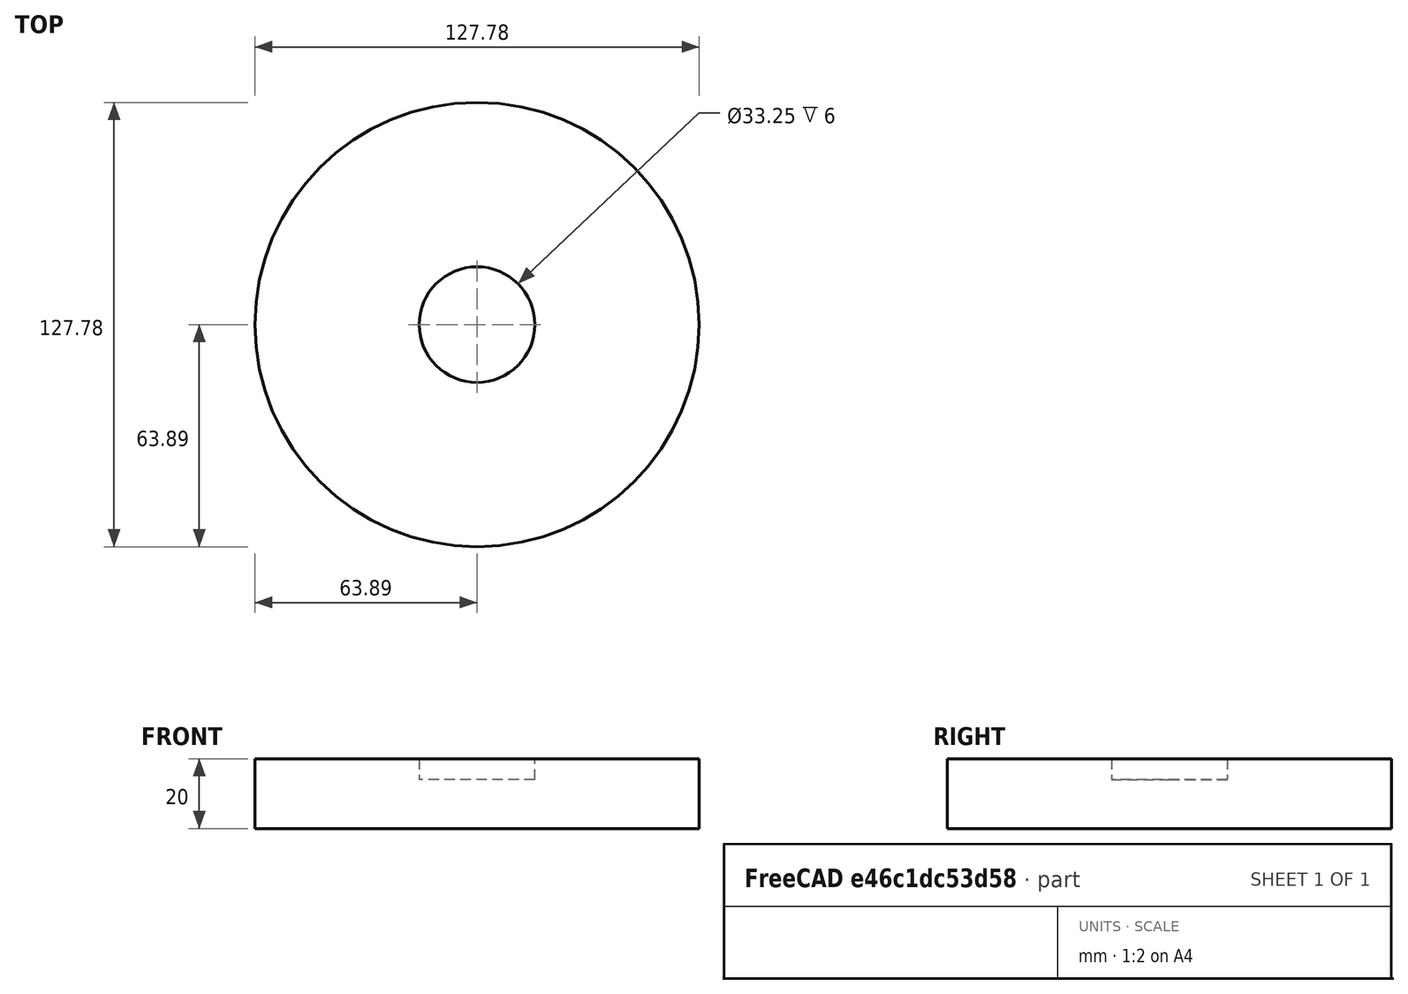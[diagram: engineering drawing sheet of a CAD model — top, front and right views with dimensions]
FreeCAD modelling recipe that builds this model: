
FCSTD DOCUMENT  (FreeCAD 0.21R33771 (Git))
Label: body_substract
License: All rights reserved
LicenseURL: http://en.wikipedia.org/wiki/All_rights_reserved
objects: Sketcher::SketchObject×2, PartDesign::Pad×2, PartDesign::Body×2, Part::Cut×1
note: 9 computed .brp shape members not serialized (recipe doc carries the construction recipe); baked Part::Feature solids carry a one-line shape summary decoded from their .brp

FEATURE [Sketcher::SketchObject] Sketch
  FullyConstrained = false
  MapMode = 5
  Support = -> [XY_Plane]
  sketch-geometry (1):
    g0: Circle CenterX=0 CenterY=0 CenterZ=0 NormalX=0 NormalY=0 NormalZ=1 AngleXU=0 Radius=63.8863
  constraints (1):
    c: Coincident(g0,g-1)
FEATURE [PartDesign::Pad] Pad
  Direction = (0,0,1)
  Length = 20
  Length2 = 10
  Profile = -> Sketch
  ReferenceAxis = -> Sketch [N_Axis]
  Refine = true
  Type = 0
FEATURE [PartDesign::Body] Body
  Group = -> [Sketch,Pad]
  Origin = -> Origin
  Tip = -> Pad
FEATURE [Sketcher::SketchObject] Sketch003
  FullyConstrained = false
  MapMode = 5
  Placement = pos=(0,0,14) rot=(0,0,1;0rad)
  sketch-geometry (1):
    g0: Circle CenterX=0 CenterY=0 CenterZ=0 NormalX=0 NormalY=0 NormalZ=1 AngleXU=0 Radius=16.6227
  constraints (1):
    c: Coincident(g0,g-1)
FEATURE [PartDesign::Pad] Pad001
  Direction = (0,0,1)
  Length = 10
  Length2 = 10
  Placement = pos=(0,0,14) rot=(0,0,1;0rad)
  Profile = -> Sketch003
  ReferenceAxis = -> Sketch003 [N_Axis]
  Refine = true
  Type = 0
FEATURE [PartDesign::Body] Body001
  Group = -> [Sketch003,Pad001]
  Origin = -> Origin001
  Tip = -> Pad001
FEATURE [Part::Cut] Cut
  Base = -> Body
  Refine = true
  Tool = -> Body001
